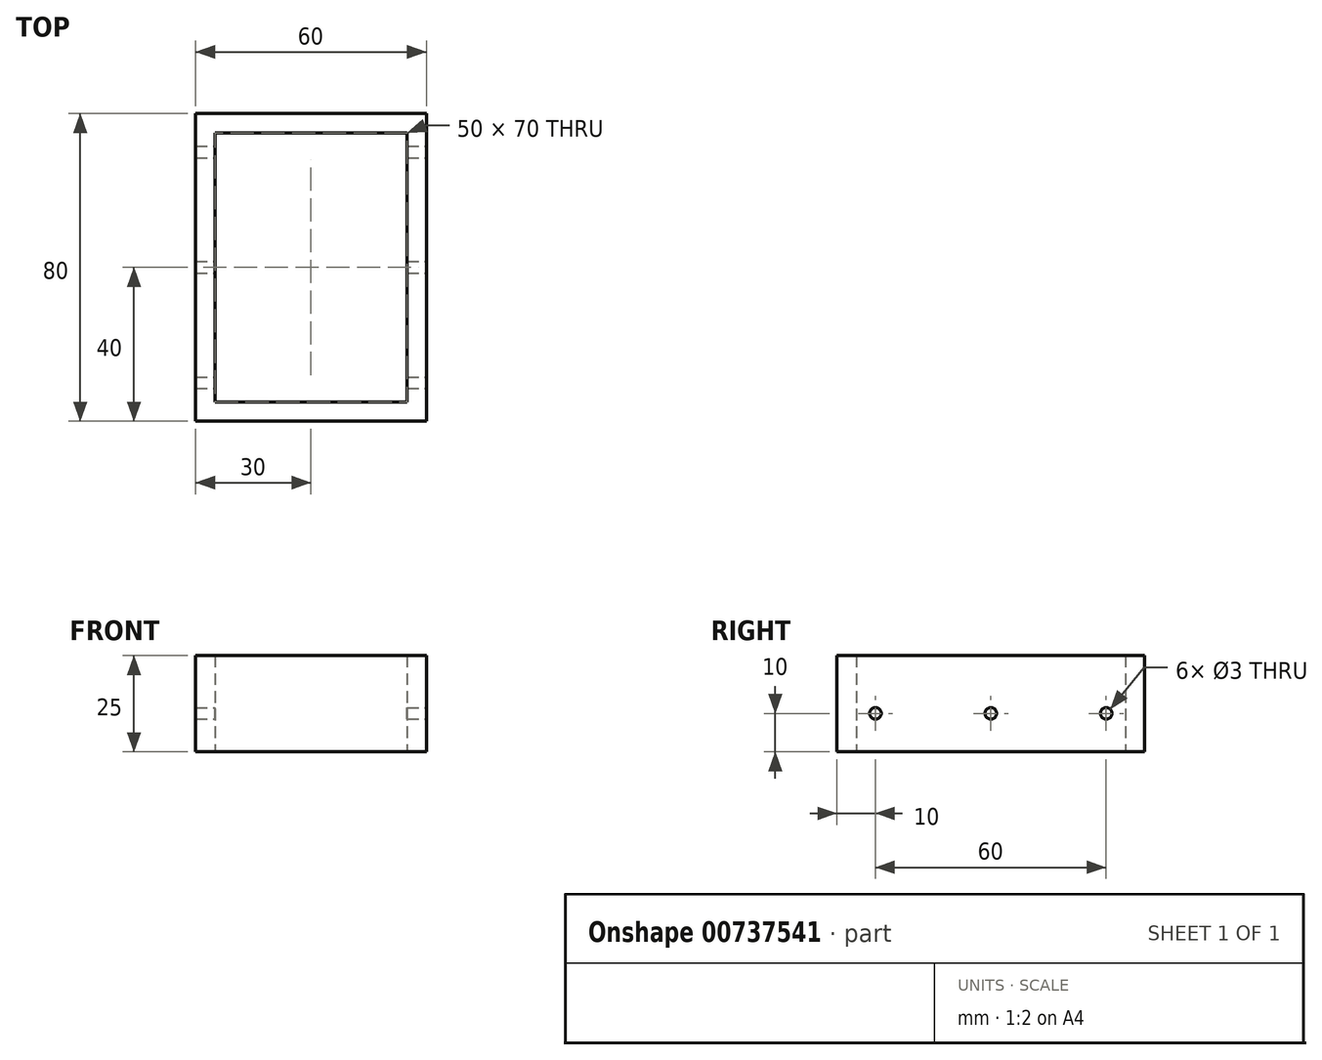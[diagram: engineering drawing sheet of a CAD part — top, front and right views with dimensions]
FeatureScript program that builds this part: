
annotation { "Feature Type Name" : "Feature", "Feature Type Description" : "" }
export const myFeature = defineFeature(function(context is Context, id is Id, definition is map)
    precondition{}
    {
        {
            var Q0;
            Q0=qCreatedBy(makeId("Top.planeOp"),FACE);
            var sketch = newSketch(context, id + "F0", { "sketchPlane" : qUnion([Q0])});
            skLineSegment(sketch, "E0.bottom", {"start": v(-30, 40) * mm, "end": v(30, 40) * mm});
            skLineSegment(sketch, "E0.top", {"start": v(-30, -40) * mm, "end": v(30, -40) * mm});
            skLineSegment(sketch, "E0.left", {"start": v(-30, 40) * mm, "end": v(-30, -40) * mm});
            skLineSegment(sketch, "E0.right", {"start": v(30, 40) * mm, "end": v(30, -40) * mm});
            skLineSegment(sketch, "E1.0", {"start": v(25, 35) * mm, "end": v(25, -35) * mm});
            skLineSegment(sketch, "E1.1", {"start": v(-25, 35) * mm, "end": v(25, 35) * mm});
            skLineSegment(sketch, "E1.2", {"start": v(-25, 35) * mm, "end": v(-25, -35) * mm});
            skLineSegment(sketch, "E1.3", {"start": v(-25, -35) * mm, "end": v(25, -35) * mm});
            skSolve(sketch);
        }
        {
            var Q0;
            Q0=makeQuery(id+"F0.imprint","IMPRINT",FACE,{"disambiguationData":[TD([[makeQuery(id+"F0.imprint","IMPRINT",EDGE,{"derivedFrom":sQuery(id+"F0.wireOp",EDGE,"E0.bottom")}),-1.0]])]});
            extrude(context, id + "F1", {"entities" : qUnion([Q0]), "depth" : 25 * mm, "offsetDistance" : 25 * mm});
        }
        {
            var Q0;
            Q0=makeQuery(id+"F1.opExtrude","SWEPT_FACE",FACE,{"disambiguationData":[OSD([sQuery(id+"F0.wireOp",EDGE,"E0.right")])]});
            var sketch = newSketch(context, id + "F2", { "sketchPlane" : qUnion([Q0])});
            skCircle(sketch, "E2", {"center": v(0, 10) * mm, "radius": 1.5 * mm});
            skCircle(sketch, "E3", {"center": v(-30, 10) * mm, "radius": 1.5 * mm});
            skCircle(sketch, "E4", {"center": v(30, 10) * mm, "radius": 1.5 * mm});
            skSolve(sketch);
        }
        {
            var Q0;
            Q0=makeQuery(id+"F2.imprint","IMPRINT",FACE,{"disambiguationData":[TD([[makeQuery(id+"F2.imprint","IMPRINT",EDGE,{"derivedFrom":sQuery(id+"F2.wireOp",EDGE,"E3")}),1.0]])]});
            var Q1;
            Q1=makeQuery(id+"F2.imprint","IMPRINT",FACE,{"disambiguationData":[TD([[makeQuery(id+"F2.imprint","IMPRINT",EDGE,{"derivedFrom":sQuery(id+"F2.wireOp",EDGE,"E2")}),1.0]])]});
            var Q2;
            Q2=makeQuery(id+"F2.imprint","IMPRINT",FACE,{"disambiguationData":[TD([[makeQuery(id+"F2.imprint","IMPRINT",EDGE,{"derivedFrom":sQuery(id+"F2.wireOp",EDGE,"E4")}),1.0]])]});
            extrude(context, id + "F3", {"entities" : qUnion([Q0, Q1, Q2]), "operationType" : NewBodyOperationType.REMOVE, "endBound" : BoundingType.THROUGH_ALL, "oppositeDirection" : true, "depth" : 25 * mm, "offsetDistance" : 25 * mm});
        }
    });
